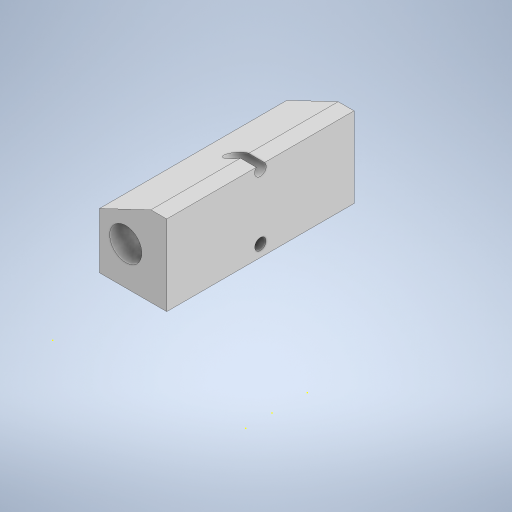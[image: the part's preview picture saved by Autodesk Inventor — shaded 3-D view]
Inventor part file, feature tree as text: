
AUTODESK INVENTOR PART (.ipt)
format: ipt  version: 2024 (Build 280153000, 153)  size: 579,584 bytes
history: native  units: mm
features: sketch x33, extrude x27, move_body x4, chamfer x3, plane x3, split x3, boolean_combine x2, other x1, fillet x1, imported_body x1
ambient origin geometry x8: Origin, YZ Plane, XZ Plane, XY Plane, X Axis, Y Axis, Z Axis, Center Point
bodies: Solid1 (feature_tree), Solid2 (feature_tree), Solid3 (feature_tree), Solid4 (feature_tree), Solid5 (feature_tree), Solid6 (feature_tree), Solid7 (feature_tree), Solid8 (feature_tree)
feature tree (78):
  other  "Repaired Geometry1"
  extrude  "Extrusion1"  Depth=16.0mm
  sketch  "Sketch2"  dims[d2=15.0mm d3=0.0mm d4=10.0mm]
  extrude  "Extrusion2"  Depth=10.0mm
  chamfer  "Chamfer1"  Distance=21.25mm
  extrude  "Extrusion3"  Depth=10.0mm TaperAngle=0.0deg
  extrude  "Extrusion4"  Depth=11.5mm TaperAngle=0.0deg
  extrude  "Extrusion5"  Depth=1.0mm TaperAngle=0.0deg
  chamfer  "Chamfer2"  Distance=6.0mm Angle=45.0deg
  sketch  "Sketch6"  dims[d14=7.0mm d15=11.5mm d16=0.0mm]
  extrude  "Extrusion6"  Depth=9.0mm
  extrude  "Extrusion7"  Depth=11.5mm TaperAngle=0.0deg
  chamfer  "Chamfer3"  Distance=11.5mm Angle=45.0deg
  sketch  "Sketch9"  dims[d26=3.3mm d27=45.25mm d28=0.0mm d29=11.5mm d30=5.5mm d31=45.0deg]
  extrude  "Extrusion8"  Depth=65.75mm TaperAngle=0.0deg
  extrude  "Extrusion9"  Depth=9.0mm TaperAngle=0.0deg
  extrude  "Extrusion10"  Depth=13.0mm TaperAngle=0.0deg
  sketch  "Sketch13"  dims[d43=24.0mm d44=21.0mm d45=0.0mm]
  extrude  "Extrusion11"  Depth=24.0mm TaperAngle=0.0deg
  extrude  "Extrusion12"  TaperAngle=0.0deg  [1 undecoded]
  extrude  "Extrusion13"  Depth=6.0mm TaperAngle=0.0deg
  plane  "Work Plane1"
  split  "Split1"
  move_body  "Move Body1"
  extrude  "Extrusion14"  Depth=0.5mm TaperAngle=0.0deg
  move_body  "Move Body2"
  fillet  "Fillet1"  Radius=10.0mm
  extrude  "Extrusion15"  Depth=10.0mm TaperAngle=0.0deg
  sketch  "Sketch19"  dims[d71=29.5mm d72=0.0mm d73=13.75mm]
  sketch  "Sketch20"  dims[d74=26.0mm d75=0.0mm d76=-5.0mm d77=0.0mm d78=0.0mm]
  extrude  "Extrusion16"  Depth=1.0mm
  extrude  "Extrusion18"  Depth=13.75mm
  extrude  "Extrusion19"  TaperAngle=0.0deg  [1 undecoded]
  sketch  "Sketch23"  dims[d86=11.5mm d87=0.0mm d88=11.5mm d89=0.0mm]
  sketch  "Sketch24"  dims[d90=4.5mm d91=38.0mm d92=0.0mm]
  extrude  "Extrusion20"  TaperAngle=0.0deg  [1 undecoded]
  plane  "Work Plane2"
  boolean_combine  "Combine1"
  split  "Split2"
  extrude  "Extrusion21"  Depth=11.5mm TaperAngle=0.0deg
  move_body  "Move Body3"
  boolean_combine  "Combine2"
  plane  "Work Plane3"
  split  "Split3"
  move_body  "Move Body4"
  extrude  "Extrusion23"  Depth=38.0mm TaperAngle=0.0deg
  extrude  "Extrusion24"  Depth=41.0mm TaperAngle=0.0deg
  extrude  "Extrusion25"  Depth=32.0mm TaperAngle=0.0deg
  extrude  "Extrusion26"  Depth=32.0mm TaperAngle=0.0deg
  extrude  "Extrusion28"  [1 undecoded]
  extrude  "Extrusion29"  [1 undecoded]
  extrude  "Extrusion30"  [1 undecoded]
  sketch  "Sketch36"
  sketch  "Sketch1"  dims[d0=36.0mm d1=16.0mm]
  sketch  "Sketch3"  dims[d5=10.0mm]
  sketch  "Sketch4"  dims[d6=3.3mm d7=21.25mm d8=0.0mm]
  sketch  "Sketch5"  dims[d9=10.0mm d10=5.5mm d11=45.0deg d12=10.0mm d13=0.0mm]
  sketch  "Sketch7"  dims[d17=3.3mm d18=1.0mm d19=0.0mm d20=6.0mm d21=11.5mm d22=45.0deg]
  sketch  "Sketch8"  dims[d23=15.0mm d24=0.0mm d25=9.0mm]
  sketch  "Sketch10"  dims[d32=2.0mm d33=65.75mm d34=0.0mm]
  sketch  "Sketch11"  dims[d35=0.5mm d36=0.0mm d37=9.0mm d38=0.0mm]
  sketch  "Sketch12"  dims[d39=0.5mm d40=0.0mm d41=13.0mm d42=0.0mm]
  sketch  "Sketch14"  dims[d46=12.25mm d47=-12.0mm d48=0.0mm d49=0.0mm]
  sketch  "Sketch15"  dims[d50=30.0mm d51=0.0mm d52=6.0mm d53=0.0mm d54=0.0mm d55=4.0mm]
  sketch  "Sketch16"  dims[d56=0.5mm d57=0.0mm d58=0.5mm d59=0.0mm d64=10.0mm d65=0.0mm]
  sketch  "Sketch17"  dims[d66=3.0mm d67=10.0mm d68=0.0mm]
  sketch  "Sketch18"  dims[d69=1.0mm d70=31.0mm]
  sketch  "Sketch22"  dims[d79=0.0mm d80=0.0mm d81=0.0mm d82=-30.0mm]
  sketch  "Sketch25"  dims[d93=5.1mm d94=41.0mm d95=0.0mm]
  sketch  "Sketch26"  dims[d98=5.5mm d99=32.0mm d100=0.0mm]
  imported_body  "Base1"
  sketch  "Sketch28"  dims[d101=32.0mm d102=0.0mm d103=32.0mm d104=0.0mm]
  sketch  "Sketch29"
  sketch  "Sketch30"
  sketch  "Sketch31"
  sketch  "Sketch33"
  sketch  "Sketch34"
  sketch  "Sketch35"
note: 6 required parameter values undecoded (feature->parameter linkage not recoverable at this tier; creation-order binding heuristic only, values carry confidence <= 0.55)
